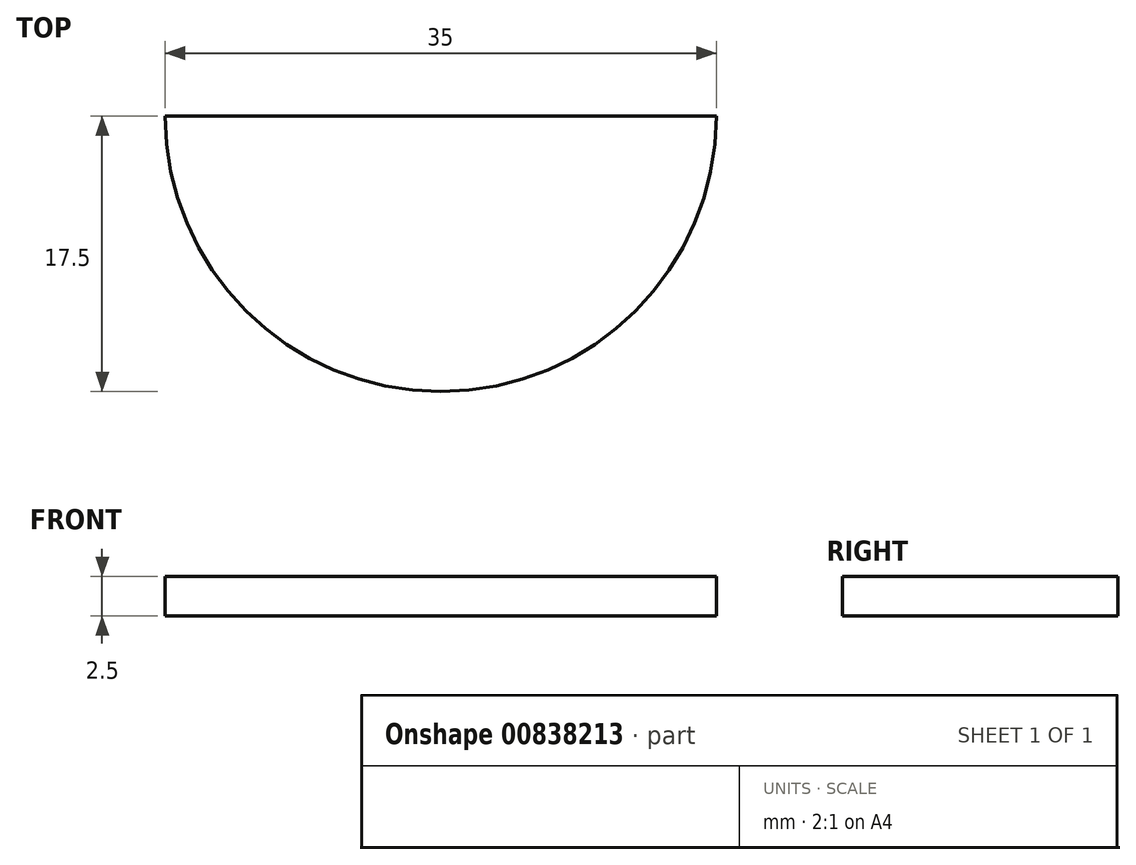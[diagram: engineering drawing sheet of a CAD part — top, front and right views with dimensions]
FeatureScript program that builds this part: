
annotation { "Feature Type Name" : "Feature", "Feature Type Description" : "" }
export const myFeature = defineFeature(function(context is Context, id is Id, definition is map)
    precondition{}
    {
        {
            var Q0;
            Q0=qCreatedBy(makeId("Top.planeOp"),FACE);
            var sketch = newSketch(context, id + "F0", { "sketchPlane" : qUnion([Q0])});
            skArc(sketch, "E0", {"start": v(-17.5, 0) * mm, "mid": v(0, -17.5) * mm, "end": v(17.5, 0) * mm});
            skLineSegment(sketch, "E1", {"start": v(-17.5, 0) * mm, "end": v(17.5, 0) * mm, "construction": true});
            skLineSegment(sketch, "E2", {"start": v(-17.5, 0) * mm, "end": v(17.5, 0) * mm});
            skPoint(sketch, "E3.orphan", {"position": v(-31.4, 0) * mm});
            skSolve(sketch);
        }
        {
            var Q0;
            Q0 = qSketchRegion(id + "F0", true);
            extrude(context, id + "F1", {"entities" : qUnion([Q0]), "depth" : 2.5 * mm, "offsetDistance" : 25 * mm});
        }
    });
